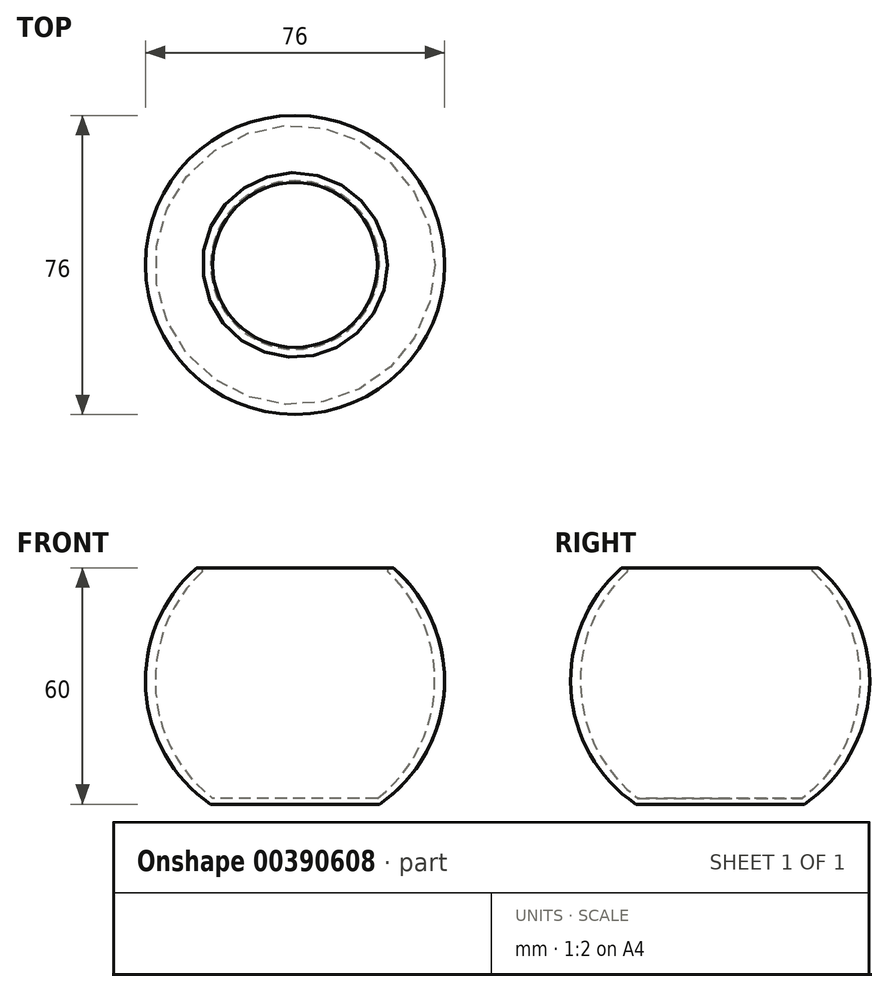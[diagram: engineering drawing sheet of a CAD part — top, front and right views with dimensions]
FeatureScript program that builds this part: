
annotation { "Feature Type Name" : "Feature", "Feature Type Description" : "" }
export const myFeature = defineFeature(function(context is Context, id is Id, definition is map)
    precondition{}
    {
        {
            var Q0;
            Q0=qCreatedBy(makeId("Front.planeOp"),FACE);
            var sketch = newSketch(context, id + "F0", { "sketchPlane" : qUnion([Q0])});
            skCircle(sketch, "E0", {"center": v(0, 0) * mm, "radius": 38 * mm});
            skLineSegment(sketch, "E1", {"start": v(-25, 28.62) * mm, "end": v(25, 28.62) * mm});
            skLineSegment(sketch, "E2", {"start": v(-21.43, -31.38) * mm, "end": v(21.43, -31.38) * mm});
            skLineSegment(sketch, "E3", {"start": v(0, 83.34) * mm, "end": v(0, -91.2) * mm, "construction": true});
            skEllipse(sketch, "E4", {"center": v(0, 0) * mm, "majorRadius": 37 * mm, "minorRadius": 35.5 * mm, "majorAxis": v(0, 1)});
            skSolve(sketch);
        }
        {
            var Q0;
            {var subQ0=sQuery(id+"F0.wireOp",EDGE,"E1");var subQ1=sQuery(id+"F0.wireOp",EDGE,"E0");var subQ2=makeQuery(id+"F0.imprint","INTERSECT",VERTEX,{"disambiguationData":[OD(1.0)],"derivedFrom":[subQ1,subQ0]});Q0=makeQuery(id+"F0.imprint","IMPRINT",FACE,{"disambiguationData":[TD([[makeQuery(id+"F0.imprint","IMPRINT",EDGE,{"disambiguationData":[TD([[subQ2,1.0]])],"derivedFrom":subQ1}),1.0]])]});}
            var Q1;
            Q1=sQuery(id+"F0.wireOp",EDGE,"E3");
            revolve(context, id + "F1", {"surfaceOperationType" : NewSurfaceOperationType.NEW, "entities" : qUnion([Q0]), "axis" : qUnion([Q1]), "revolveType" : RevolveType.FULL});
        }
        {
            var Q0;
            Q0=makeQuery(id+"F1.opRevolve","SWEPT_FACE",FACE,{"disambiguationData":[OSD([sQuery(id+"F0.wireOp",EDGE,"E2")])]});
            var sketch = newSketch(context, id + "F2", { "sketchPlane" : qUnion([Q0])});
            skCircle(sketch, "E5", {"center": v(0, 0) * mm, "radius": 21.5 * mm});
            skSolve(sketch);
        }
        {
            var Q0;
            Q0=makeQuery(id+"F2.imprint","IMPRINT",FACE,{"disambiguationData":[TD([[makeQuery(id+"F2.imprint","IMPRINT",EDGE,{"derivedFrom":makeQuery(id+"F1.opRevolve","SWEPT_EDGE",EDGE,{"disambiguationData":[OSD([sQuery(id+"F0.wireOp",EDGE,"E2"),sQuery(id+"F0.wireOp",EDGE,"MhfCv9Pj-1ALy-Ekvo-Mi4J-g2yaFm380eha")])]})}),-1.0]])]});
            var Q1;
            {var subQ0=sQuery(id+"F0.wireOp",EDGE,"E2");Q1=makeQuery(id+"F2.imprint","IMPRINT",FACE,{"disambiguationData":[TD([[makeQuery(id+"F2.imprint","IMPRINT",EDGE,{"derivedFrom":makeQuery(id+"F1.opRevolve","SWEPT_EDGE",EDGE,{"disambiguationData":[OSD([sQuery(id+"F0.wireOp",EDGE,"E0"),subQ0])]})}),-1.0]])]});}
            extrude(context, id + "F3", {"entities" : qUnion([Q0, Q1]), "operationType" : NewBodyOperationType.ADD, "oppositeDirection" : true, "depth" : 1.5 * mm, "offsetDistance" : 25 * mm});
        }
        {
            var Q0;
            Q0=makeQuery(id+"F1.opRevolve","SWEPT_EDGE",EDGE,{"disambiguationData":[OSD([sQuery(id+"F0.wireOp",EDGE,"E1"),sQuery(id+"F0.wireOp",EDGE,"E4")])]});
            var Q1;
            Q1=makeQuery(id+"F1.opRevolve","SWEPT_EDGE",EDGE,{"disambiguationData":[OSD([sQuery(id+"F0.wireOp",EDGE,"E0"),sQuery(id+"F0.wireOp",EDGE,"E1")])]});
            fillet(context, id + "F4", {"entities" : qUnion([Q0, Q1]), "radius" : 0.6 * mm, "tangentPropagation" : true, "defaultsChanged" : true, "vertexSettings" : [], "allowEdgeOverflow" : false});
        }
    });
